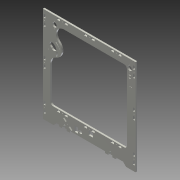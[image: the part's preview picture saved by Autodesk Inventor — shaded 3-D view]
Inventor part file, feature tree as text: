
AUTODESK INVENTOR PART (.ipt)
format: ipt  version: 2013 (Build 170138000, 138)  size: 713,728 bytes
history: native  units: mm
features: sketch x11, extrude x7, plane x6, revolve x3, fillet x3, projected_geometry x3
ambient origin geometry x8: Origin, YZ Plane, XZ Plane, XY Plane, X Axis, Y Axis, Z Axis, Center Point
bodies: Solid1 (feature_tree)
feature tree (33):
  extrude  "Extrusion1"  Depth=12.0mm
  extrude  "Extrusion2"  Depth=7.8mm
  plane  "Work Plane1"
  sketch  "Sketch6"  dims[d6=7.8mm d7=3.2mm d8=135.0mm]
  plane  "Work Plane2"
  revolve  "Revolution1"  [1 undecoded]
  plane  "Work Plane4"
  fillet  "Fillet3"  Radius=135.0mm
  revolve  "Revolution2"  [1 undecoded]
  plane  "Work Plane6"
  revolve  "Revolution3"  [1 undecoded]
  fillet  "Fillet4"  Radius=144.4mm
  fillet  "Fillet5"  Radius=12.0mm
  extrude  "Extrusion5"  Depth=7.8mm
  extrude  "Extrusion6"  Depth=6.4mm
  extrude  "Extrusion7"  Depth=344.1mm
  extrude  "Extrusion8"  Depth=3.0mm
  extrude  "Extrusion9"  Depth=6.2mm
  sketch  "Sketch1"  dims[d0=12.0mm d2=12.0mm]
  sketch  "Sketch2"  dims[d3=6.4mm d5=7.8mm]
  sketch  "Sketch7"  dims[d9=7.8mm d10=7.8mm]
  projected_geometry  "Projected Loop1"
  plane  "Work Plane3"
  sketch  "Sketch8"  dims[d11=12.0mm d12=12.0mm d14=144.4mm d15=12.0mm]
  projected_geometry  "Projected Loop2"
  plane  "Work Plane5"
  sketch  "Sketch9"  dims[d16=7.8mm d17=7.8mm]
  projected_geometry  "Projected Loop3"
  sketch  "Sketch11"  dims[d18=12.0mm d19=6.4mm]
  sketch  "Sketch12"  dims[d20=3.2mm d21=344.1mm]
  sketch  "Sketch13"  dims[d22=354.4mm d23=3.0mm]
  sketch  "Sketch15"  dims[d24=6.2mm d25=6.2mm]
  sketch  "Sketch16"  dims[d26=19.4mm d27=54.4mm d28=35.0mm d29=6.4mm d30=12.0mm d31=7.8mm d32=7.8mm d33=12.0mm d34=3.2mm d35=12.0mm d36=7.8mm d37=7.8mm d38=12.0mm d39=12.0mm d40=7.8mm d41=7.8mm d42=12.0mm d43=100.0mm d44=100.0mm d45=6.2mm d47=6.4mm d48=3.2mm d49=53.2mm d50=11.0mm d51=11.0mm d52=16.1mm d53=31.0mm d54=21.7mm d55=6.0mm d56=9.5mm d57=19.0mm d58=52.95mm d59=1.25mm d60=6.0mm d61=15.0mm d62=88.912448mm d63=43.4mm d74=11.298786mm d75=135.0deg d76=7.0mm d77=1.8mm d78=1.8mm d79=1.25mm d80=3.0mm d81=1.25mm d82=12.4mm d83=11.8mm d84=0.3mm d85=35.0mm d87=6.1mm d88=12.4mm d89=3.0mm d90=1.25mm d91=1.25mm d92=170.0mm d93=11.8mm d94=11.8mm d95=40.0mm d96=6.0mm d97=6.1mm d99=6.1mm d100=32.0mm d101=28.0mm d102=70.0mm d103=28.0mm d104=59.4mm d105=10.0mm d106=160.0mm d107=6.4mm d108=12.0mm d109=12.0mm d111=3.2mm d112=7.8mm d113=7.8mm d114=17.548658mm d116=6.981317mm d117=12.5mm d118=16.0mm d119=47.0mm d120=2.8mm d121=12.3mm d122=19.3mm d123=2.676575mm d124=9.059984mm d125=9.645837mm d126=8.0mm d130=6.0mm d131=0.0mm d134=162.65mm d135=6.1mm d136=92.52408mm d138=10.62808mm d140=16.0mm d141=16.0mm d142=8.0mm d143=19.401659mm d144=2.0mm d145=5.0mm d147=43.0mm d148=14.0mm d149=2.0mm d150=10.0mm d151=0.0mm d152=3.0mm d153=3.0mm d154=3.0mm d155=3.0mm d156=3.0mm d157=12.5mm d158=87.5mm d172=-1.745329mm d173=3.0mm d175=31.0mm d176=1.5mm d177=30.0deg d178=-7.853982mm d179=3.0mm d181=1.5mm d182=43.85mm d183=30.0deg d186=1.4mm d187=-1.745329mm d188=18.0mm d190=1.5mm d191=13.0mm d192=9.599311mm d193=15.0deg d194=8.0mm d195=1.4mm d196=5.0mm d197=31.5mm d198=8.0mm d199=2.0mm d200=38.0mm d201=103.204936mm d202=64.435595mm d203=10.0mm d204=0.0mm d205=29.110089mm d206=60.0mm d208=6.0mm d209=0.0mm d210=16.0mm d212=6.0mm d213=0.0mm d214=6.0mm d215=0.0mm d216=3.0mm d218=3.0mm d219=12.0mm d220=12.0mm d221=6.0mm d222=0.0mm d224=6.0mm]
note: 3 required parameter values undecoded (feature->parameter linkage not recoverable at this tier; creation-order binding heuristic only, values carry confidence <= 0.55)
